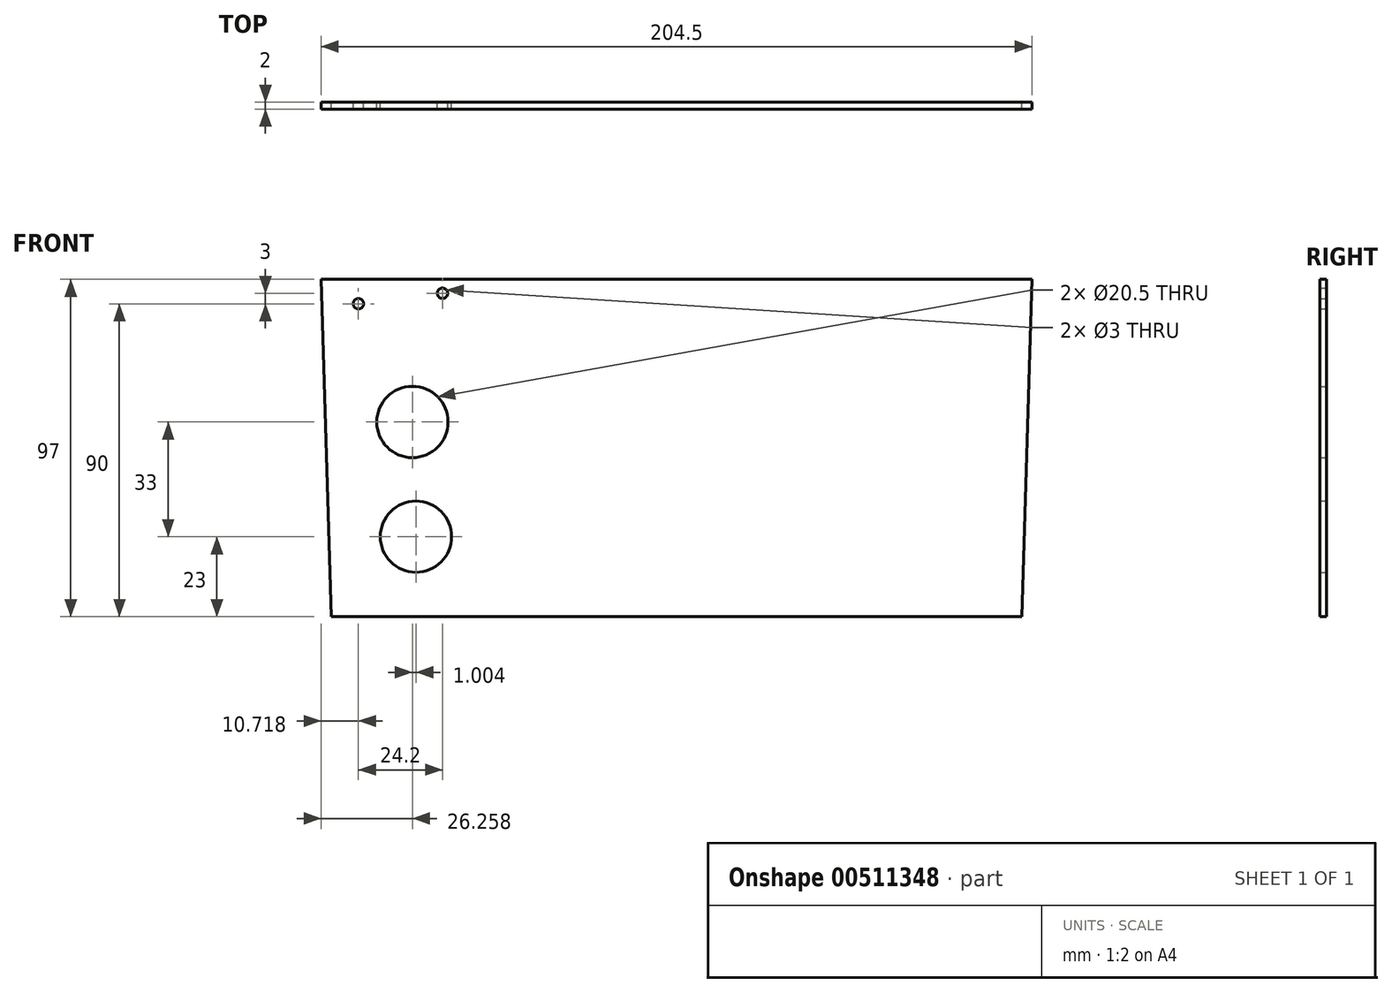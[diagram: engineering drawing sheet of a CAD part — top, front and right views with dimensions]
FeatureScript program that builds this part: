
annotation { "Feature Type Name" : "Feature", "Feature Type Description" : "" }
export const myFeature = defineFeature(function(context is Context, id is Id, definition is map)
    precondition{}
    {
        {
            var Q0;
            Q0=qCreatedBy(makeId("Front.planeOp"),FACE);
            var sketch = newSketch(context, id + "F0", { "sketchPlane" : qUnion([Q0])});
            skLineSegment(sketch, "E0", {"start": v(0, 0) * mm, "end": v(-99.3, 0) * mm});
            skLineSegment(sketch, "E1", {"start": v(0, 97) * mm, "end": v(-102.25, 97) * mm});
            skLineSegment(sketch, "E2", {"start": v(-102.25, 97) * mm, "end": v(-99.3, 0) * mm});
            skCircle(sketch, "E3", {"center": v(-74.99, 23) * mm, "radius": 10.25 * mm});
            skLineSegment(sketch, "E4.MirrorCS", {"start": v(0, 0) * mm, "end": v(99.3, 0) * mm});
            skLineSegment(sketch, "E5.MirrorCS", {"start": v(0, 97) * mm, "end": v(102.25, 97) * mm});
            skLineSegment(sketch, "E6.MirrorCS", {"start": v(102.25, 97) * mm, "end": v(99.3, 0) * mm});
            skCircle(sketch, "E7", {"center": v(-76, 56) * mm, "radius": 10.25 * mm});
            skCircle(sketch, "E8", {"center": v(-91.53, 90) * mm, "radius": 1.5 * mm});
            skCircle(sketch, "E9", {"center": v(-67.33, 93) * mm, "radius": 1.5 * mm});
            skSolve(sketch);
        }
        {
            var Q0;
            Q0 = qSketchRegion(id + "F0", true);
            extrude(context, id + "F1", {"entities" : qUnion([Q0]), "depth" : 2 * mm, "offsetDistance" : 25 * mm});
        }
    });
